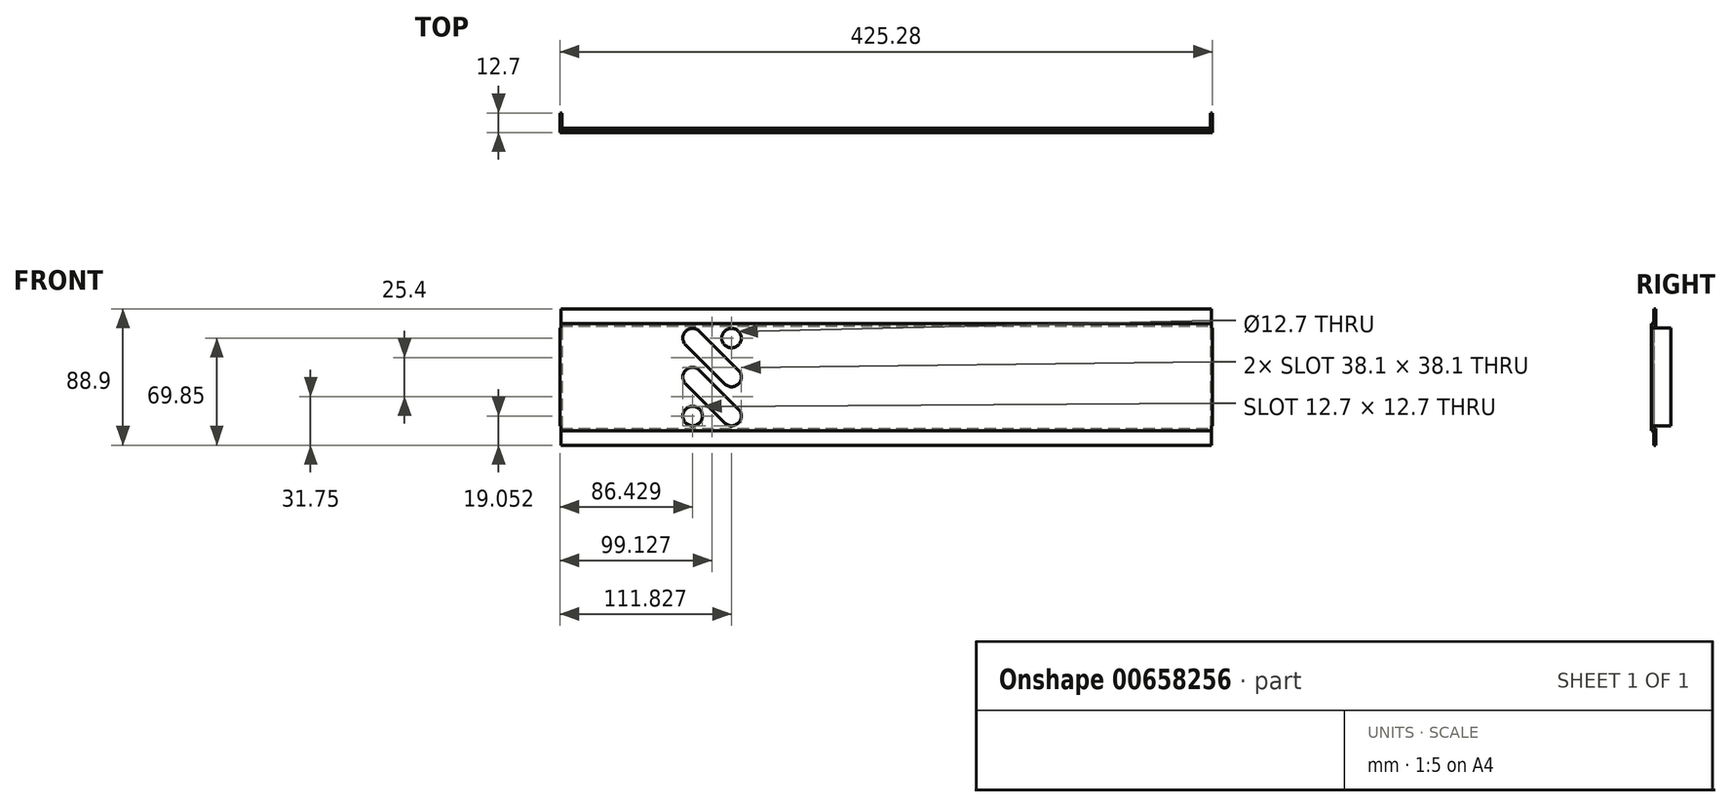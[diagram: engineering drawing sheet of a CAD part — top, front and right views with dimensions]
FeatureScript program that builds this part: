
annotation { "Feature Type Name" : "Feature", "Feature Type Description" : "" }
export const myFeature = defineFeature(function(context is Context, id is Id, definition is map)
    precondition{}
    {
        {
            var Q0;
            Q0=qCreatedBy(makeId("Front.planeOp"),FACE);
            var sketch = newSketch(context, id + "F0", { "sketchPlane" : qUnion([Q0])});
            skLineSegment(sketch, "E0.bottom", {"start": v(-211.94, 34.92) * mm, "end": v(211.94, 34.92) * mm});
            skLineSegment(sketch, "E0.top", {"start": v(-211.94, -34.92) * mm, "end": v(211.94, -34.92) * mm});
            skLineSegment(sketch, "E0.left", {"start": v(-211.94, 34.92) * mm, "end": v(-211.94, -34.92) * mm});
            skLineSegment(sketch, "E0.right", {"start": v(211.94, 34.92) * mm, "end": v(211.94, -34.92) * mm});
            skPoint(sketch, "E1", {"position": v(0, 34.92) * mm});
            skPoint(sketch, "E2", {"position": v(-211.94, 0) * mm});
            skLineSegment(sketch, "E3", {"start": v(-211.94, 31.75) * mm, "end": v(211.94, 31.75) * mm, "construction": true});
            skLineSegment(sketch, "E4", {"start": v(-211.94, -31.75) * mm, "end": v(211.94, -31.75) * mm, "construction": true});
            skLineSegment(sketch, "E5", {"start": v(-211.94, 31.75) * mm, "end": v(-211.94, -31.75) * mm, "construction": true});
            skLineSegment(sketch, "E6", {"start": v(-132.56, 31.75) * mm, "end": v(-132.56, -31.75) * mm, "construction": true});
            skLineSegment(sketch, "E7", {"start": v(-94.46, 31.75) * mm, "end": v(-94.46, -31.75) * mm, "construction": true});
            skLineSegment(sketch, "E8", {"start": v(-132.56, 31.75) * mm, "end": v(-94.46, -6.35) * mm, "construction": true});
            skLineSegment(sketch, "E9", {"start": v(-94.46, -31.75) * mm, "end": v(-132.56, 6.35) * mm, "construction": true});
            skLineSegment(sketch, "E10", {"start": v(-132.56, 15.33) * mm, "end": v(-94.46, -22.77) * mm});
            skLineSegment(sketch, "E11", {"start": v(-132.56, -2.63) * mm, "end": v(-103.44, -31.75) * mm});
            skLineSegment(sketch, "E12", {"start": v(-94.46, -15.33) * mm, "end": v(-132.56, 22.77) * mm});
            skLineSegment(sketch, "E13", {"start": v(-123.58, 31.75) * mm, "end": v(-94.46, 2.63) * mm});
            skArc(sketch, "E14", {"start": v(-121.72, 29.9) * mm, "mid": v(-130.7, 29.9) * mm, "end": v(-130.7, 20.9) * mm});
            skArc(sketch, "E15", {"start": v(-105.3, -4.5) * mm, "mid": v(-96.32, -4.5) * mm, "end": v(-96.32, 4.5) * mm});
            skArc(sketch, "E16", {"start": v(-121.72, 4.5) * mm, "mid": v(-130.7, 4.5) * mm, "end": v(-130.7, -4.5) * mm});
            skArc(sketch, "E17", {"start": v(-105.3, -29.9) * mm, "mid": v(-96.32, -29.9) * mm, "end": v(-96.32, -20.9) * mm});
            skLineSegment(sketch, "E18", {"start": v(-132.56, -10.07) * mm, "end": v(-110.88, -31.75) * mm});
            skLineSegment(sketch, "E19", {"start": v(-132.56, -28.03) * mm, "end": v(-128.84, -31.75) * mm});
            skArc(sketch, "E20", {"start": v(-121.72, -20.9) * mm, "mid": v(-130.7, -20.9) * mm, "end": v(-130.7, -29.89) * mm});
            skArc(sketch, "E21", {"start": v(-130.7, -29.9) * mm, "mid": v(-121.72, -29.9) * mm, "end": v(-121.72, -20.9) * mm});
            skPoint(sketch, "E22", {"position": v(-100.81, 25.4) * mm});
            skCircle(sketch, "E23", {"center": v(-100.81, 25.4) * mm, "radius": 6.35 * mm});
            skSolve(sketch);
        }
        {
            var Q0;
            Q0=qSketchRegion(id+"F0",true);
            extrude(context, id + "F1", {"entities" : qUnion([Q0]), "depth" : 1.4 * mm, "offsetDistance" : 25 * mm});
        }
        {
            var Q0;
            Q0=makeQuery(id+"F1.opExtrude","CAP_FACE",FACE,{"disambiguationData":[OSD([sQuery(id+"F0.wireOp",EDGE,"E0.bottom"),sQuery(id+"F0.wireOp",EDGE,"E0.top"),sQuery(id+"F0.wireOp",EDGE,"E0.left"),sQuery(id+"F0.wireOp",EDGE,"E0.right"),sQuery(id+"F0.wireOp",EDGE,"E10"),sQuery(id+"F0.wireOp",EDGE,"E11"),sQuery(id+"F0.wireOp",EDGE,"E12"),sQuery(id+"F0.wireOp",EDGE,"E13"),sQuery(id+"F0.wireOp",EDGE,"E14"),sQuery(id+"F0.wireOp",EDGE,"E15"),sQuery(id+"F0.wireOp",EDGE,"E16"),sQuery(id+"F0.wireOp",EDGE,"E17"),sQuery(id+"F0.wireOp",EDGE,"E18"),sQuery(id+"F0.wireOp",EDGE,"E19"),sQuery(id+"F0.wireOp",EDGE,"E20"),sQuery(id+"F0.wireOp",EDGE,"E21"),sQuery(id+"F0.wireOp",EDGE,"E23")])],"isStart":true});
            var sketch = newSketch(context, id + "F2", { "sketchPlane" : qUnion([Q0])});
            skLineSegment(sketch, "E24.bottom", {"start": v(211.94, 33.34) * mm, "end": v(-211.94, 33.34) * mm});
            skLineSegment(sketch, "E24.top", {"start": v(211.94, 44.45) * mm, "end": v(-211.94, 44.45) * mm});
            skLineSegment(sketch, "E24.left", {"start": v(211.94, 33.34) * mm, "end": v(211.94, 44.45) * mm});
            skLineSegment(sketch, "E24.right", {"start": v(-211.94, 33.34) * mm, "end": v(-211.94, 44.45) * mm});
            skLineSegment(sketch, "E25.bottom", {"start": v(211.94, -33.34) * mm, "end": v(-211.94, -33.34) * mm});
            skLineSegment(sketch, "E25.top", {"start": v(211.94, -44.45) * mm, "end": v(-211.94, -44.45) * mm});
            skLineSegment(sketch, "E25.left", {"start": v(211.94, -33.34) * mm, "end": v(211.94, -44.45) * mm});
            skLineSegment(sketch, "E25.right", {"start": v(-211.94, -33.34) * mm, "end": v(-211.94, -44.45) * mm});
            skSolve(sketch);
        }
        {
            var Q0;
            Q0 = qSketchRegion(id + "F2", true);
            extrude(context, id + "F3", {"entities" : qUnion([Q0]), "operationType" : NewBodyOperationType.ADD, "depth" : 1.4 * mm, "offsetDistance" : 25.4 * mm});
        }
        {
            var Q0;
            Q0=makeQuery(id+"F1.opExtrude","CAP_FACE",FACE,{"disambiguationData":[OSD([sQuery(id+"F0.wireOp",EDGE,"E0.bottom"),sQuery(id+"F0.wireOp",EDGE,"E0.top"),sQuery(id+"F0.wireOp",EDGE,"E0.left"),sQuery(id+"F0.wireOp",EDGE,"E0.right"),sQuery(id+"F0.wireOp",EDGE,"E10"),sQuery(id+"F0.wireOp",EDGE,"E11"),sQuery(id+"F0.wireOp",EDGE,"E12"),sQuery(id+"F0.wireOp",EDGE,"E13"),sQuery(id+"F0.wireOp",EDGE,"E14"),sQuery(id+"F0.wireOp",EDGE,"E15"),sQuery(id+"F0.wireOp",EDGE,"E16"),sQuery(id+"F0.wireOp",EDGE,"E17"),sQuery(id+"F0.wireOp",EDGE,"E18"),sQuery(id+"F0.wireOp",EDGE,"E19"),sQuery(id+"F0.wireOp",EDGE,"E20"),sQuery(id+"F0.wireOp",EDGE,"E21"),sQuery(id+"F0.wireOp",EDGE,"E23")])],"isStart":false});
            var sketch = newSketch(context, id + "F4", { "sketchPlane" : qUnion([Q0])});
            skLineSegment(sketch, "E26.bottom", {"start": v(-211.24, 31.88) * mm, "end": v(-212.64, 31.88) * mm});
            skLineSegment(sketch, "E26.top", {"start": v(-211.24, -31.88) * mm, "end": v(-212.64, -31.88) * mm});
            skLineSegment(sketch, "E26.left", {"start": v(-211.24, 31.88) * mm, "end": v(-211.24, -31.88) * mm});
            skLineSegment(sketch, "E26.right", {"start": v(-212.64, 31.88) * mm, "end": v(-212.64, -31.88) * mm});
            skLineSegment(sketch, "E27.bottom", {"start": v(211.24, 31.88) * mm, "end": v(212.64, 31.88) * mm});
            skLineSegment(sketch, "E27.top", {"start": v(211.24, -31.88) * mm, "end": v(212.64, -31.88) * mm});
            skLineSegment(sketch, "E27.left", {"start": v(211.24, 31.88) * mm, "end": v(211.24, -31.88) * mm});
            skLineSegment(sketch, "E27.right", {"start": v(212.64, 31.88) * mm, "end": v(212.64, -31.88) * mm});
            skPoint(sketch, "E28", {"position": v(-211.94, 31.88) * mm});
            skPoint(sketch, "E29", {"position": v(211.94, 31.88) * mm});
            skSolve(sketch);
        }
        {
            var Q0;
            Q0 = qSketchRegion(id + "F4", true);
            extrude(context, id + "F5", {"entities" : qUnion([Q0]), "operationType" : NewBodyOperationType.ADD, "oppositeDirection" : true, "depth" : 12.7 * mm, "offsetDistance" : 25.4 * mm});
        }
    });
